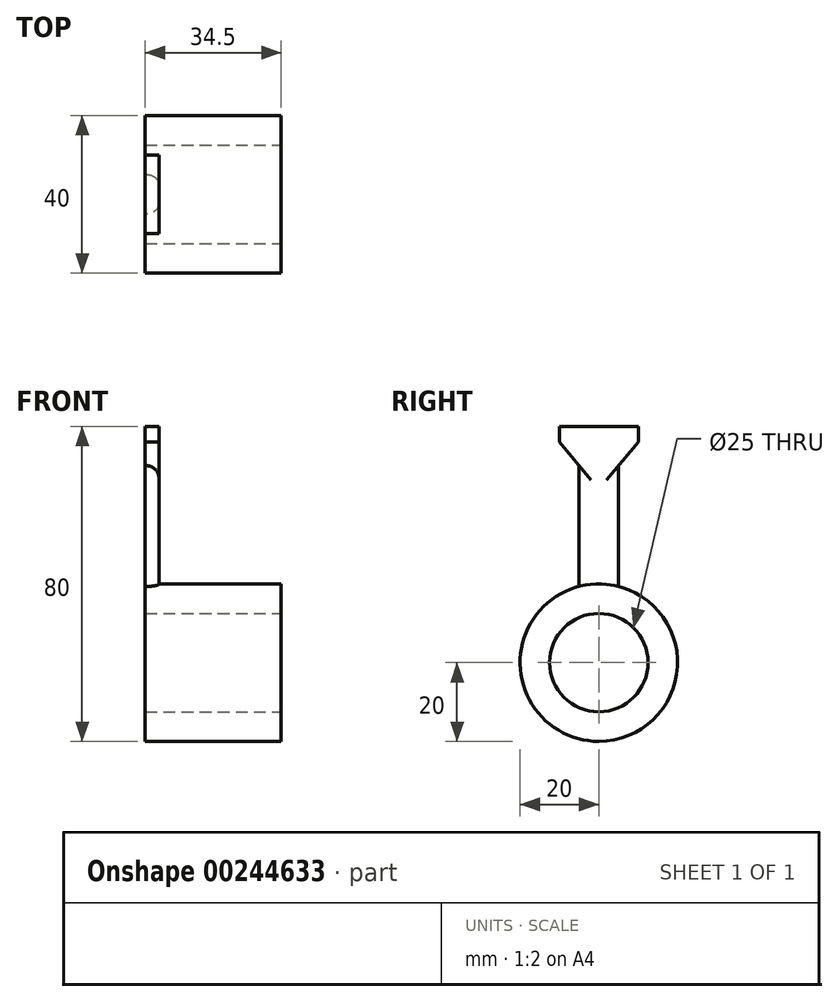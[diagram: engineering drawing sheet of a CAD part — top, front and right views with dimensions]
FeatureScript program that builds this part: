
annotation { "Feature Type Name" : "Feature", "Feature Type Description" : "" }
export const myFeature = defineFeature(function(context is Context, id is Id, definition is map)
    precondition{}
    {
        {
            var Q0;
            Q0=qCreatedBy(makeId("Right.planeOp"),FACE);
            var sketch = newSketch(context, id + "F0", { "sketchPlane" : qUnion([Q0])});
            skLineSegment(sketch, "E0", {"start": v(0, -25) * mm, "end": v(-5, -25) * mm, "construction": true});
            skLineSegment(sketch, "E1", {"start": v(-5, -25) * mm, "end": v(-5, -9.96) * mm});
            skLineSegment(sketch, "E2", {"start": v(-5, -9.96) * mm, "end": v(-10, -4) * mm});
            skLineSegment(sketch, "E3", {"start": v(-10, -4) * mm, "end": v(-10, 0) * mm});
            skLineSegment(sketch, "E4", {"start": v(-10, 0) * mm, "end": v(0, 0) * mm});
            skLineSegment(sketch, "E5", {"start": v(0, 0) * mm, "end": v(0, -25) * mm});
            skArc(sketch, "E6", {"start": v(0, -80) * mm, "mid": v(-19.84, -62.52) * mm, "end": v(-5, -40.64) * mm});
            skLineSegment(sketch, "E7", {"start": v(-5, -25) * mm, "end": v(-5, -40.64) * mm});
            skLineSegment(sketch, "E8", {"start": v(0, -25) * mm, "end": v(0, -80) * mm});
            skSolve(sketch);
        }
        {
            var Q0;
            Q0=makeQuery(id+"F0.imprint","IMPRINT",FACE,{"disambiguationData":[TD([[makeQuery(id+"F0.imprint","IMPRINT",EDGE,{"derivedFrom":sQuery(id+"F0.wireOp",EDGE,"E1")}),-1.0]])]});
            extrude(context, id + "F1", {"entities" : qUnion([Q0]), "depth" : 3.5 * mm});
        }
        {
            var Q0;
            Q0=makeQuery(id+"F1.opExtrude","CAP_FACE",FACE,{"disambiguationData":[OSD([sQuery(id+"F0.wireOp",EDGE,"E1"),sQuery(id+"F0.wireOp",EDGE,"E2"),sQuery(id+"F0.wireOp",EDGE,"E3"),sQuery(id+"F0.wireOp",EDGE,"E4"),sQuery(id+"F0.wireOp",EDGE,"E5"),sQuery(id+"F0.wireOp",EDGE,"E6"),sQuery(id+"F0.wireOp",EDGE,"E7"),sQuery(id+"F0.wireOp",EDGE,"E8")])],"isStart":false});
            var sketch = newSketch(context, id + "F2", { "sketchPlane" : qUnion([Q0])});
            skCircle(sketch, "E9", {"center": v(0, -60) * mm, "radius": 20 * mm});
            skSolve(sketch);
        }
        {
            var Q0;
            Q0=makeQuery(id+"F1.opExtrude","SWEPT_BODY",BODY,{"disambiguationData":[OSD([sQuery(id+"F0.wireOp",EDGE,"E1"),sQuery(id+"F0.wireOp",EDGE,"E2"),sQuery(id+"F0.wireOp",EDGE,"E3"),sQuery(id+"F0.wireOp",EDGE,"E4"),sQuery(id+"F0.wireOp",EDGE,"E5"),sQuery(id+"F0.wireOp",EDGE,"E6"),sQuery(id+"F0.wireOp",EDGE,"E7"),sQuery(id+"F0.wireOp",EDGE,"E8")])]});
            var Q1;
            Q1=makeQuery(id+"F1.opExtrude","SWEPT_FACE",FACE,{"disambiguationData":[OSD([sQuery(id+"F0.wireOp",EDGE,"E5"),sQuery(id+"F0.wireOp",EDGE,"E8")])]});
            mirror(context, id + "F3", {"operationType" : NewBodyOperationType.ADD, "entities" : qUnion([Q0]), "mirrorPlane" : qUnion([Q1])});
        }
        {
            var Q0;
            Q0 = qSketchRegion(id + "F2", true);
            extrude(context, id + "F4", {"entities" : qUnion([Q0]), "operationType" : NewBodyOperationType.ADD, "depth" : 31 * mm});
        }
        {
            var Q0;
            Q0=makeQuery(id+"F4.opExtrude","CAP_FACE",FACE,{"disambiguationData":[OSD([sQuery(id+"F2.wireOp",EDGE,"E9")])],"isStart":false});
            var sketch = newSketch(context, id + "F5", { "sketchPlane" : qUnion([Q0])});
            skPoint(sketch, "E10", {"position": v(0, -60) * mm});
            skSolve(sketch);
        }
        {
            var Q0;
            Q0=sQuery(id+"F5.wireOp",VERTEX,"E10");
            var Q1;
            Q1=makeQuery(id+"F1.opExtrude","SWEPT_BODY",BODY,{"disambiguationData":[OSD([sQuery(id+"F0.wireOp",EDGE,"E1"),sQuery(id+"F0.wireOp",EDGE,"E2"),sQuery(id+"F0.wireOp",EDGE,"E3"),sQuery(id+"F0.wireOp",EDGE,"E4"),sQuery(id+"F0.wireOp",EDGE,"E5"),sQuery(id+"F0.wireOp",EDGE,"E6"),sQuery(id+"F0.wireOp",EDGE,"E7"),sQuery(id+"F0.wireOp",EDGE,"E8")])]});
            hole(context, id + "F6", {"style" : HoleStyle.SIMPLE, "endStyle" : HoleEndStyle.THROUGH, "holeDiameter" : 25 * mm, "tappedDepth" : 12 * mm, "tapClearance" : 3, "startFromSketch" : true, "locations" : qUnion([Q0]), "scope" : qUnion([Q1])});
        }
        {
            var Q0;
            Q0=makeQuery(id+"F3.opPattern","COPY",EDGE,{"derivedFrom":makeQuery(id+"F1.opExtrude","CAP_EDGE",EDGE,{"disambiguationData":[OSD([sQuery(id+"F0.wireOp",EDGE,"E1"),sQuery(id+"F0.wireOp",EDGE,"E7")])],"isStart":false}),"instanceName":"1"});
            var Q1;
            Q1=makeQuery(id+"F1.opExtrude","CAP_EDGE",EDGE,{"disambiguationData":[OSD([sQuery(id+"F0.wireOp",EDGE,"E1"),sQuery(id+"F0.wireOp",EDGE,"E7")])],"isStart":false});
            fillet(context, id + "F7", {"entities" : qUnion([Q0, Q1]), "radius" : 3 * mm, "tangentPropagation" : true, "allowEdgeOverflow" : false});
        }
    });
